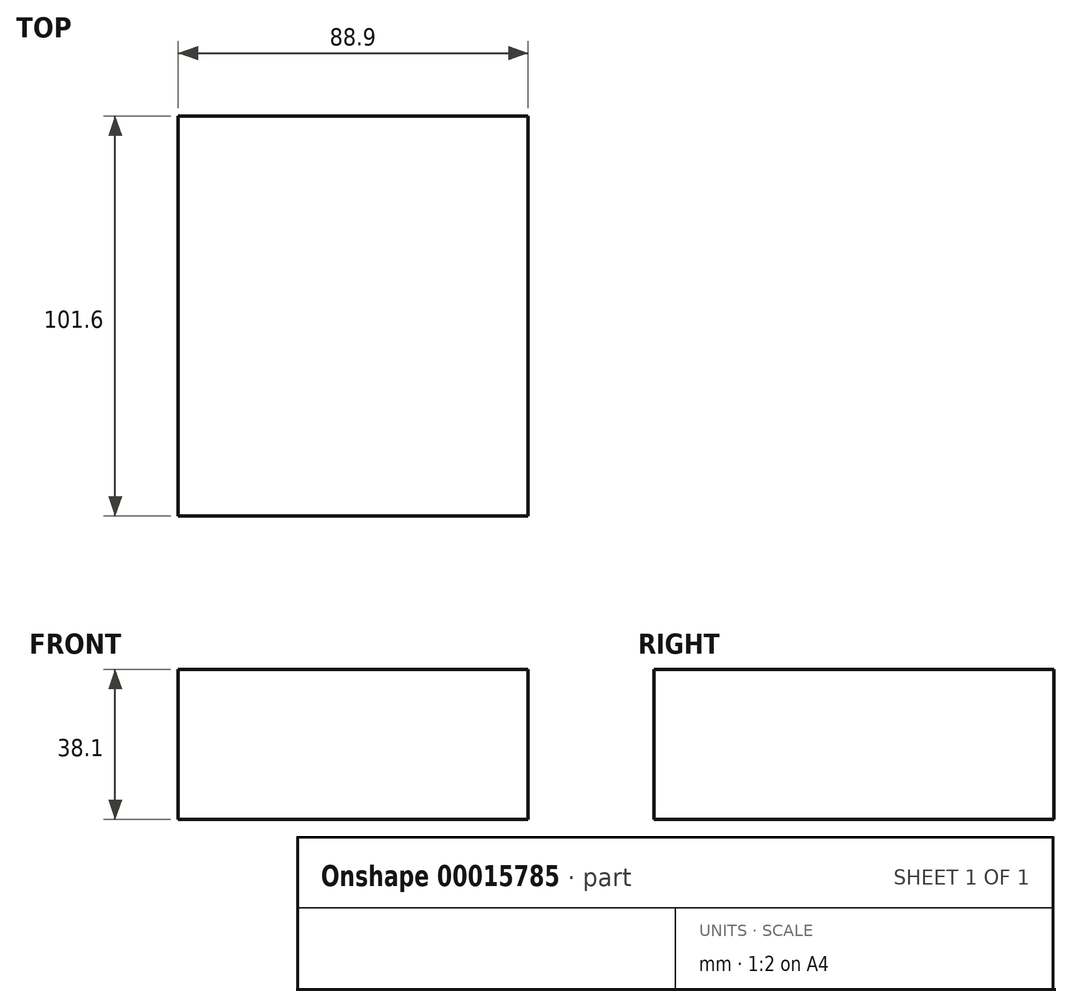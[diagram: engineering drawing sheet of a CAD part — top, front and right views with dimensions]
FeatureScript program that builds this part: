
annotation { "Feature Type Name" : "Feature", "Feature Type Description" : "" }
export const myFeature = defineFeature(function(context is Context, id is Id, definition is map)
    precondition{}
    {
        {
            var Q0;
            Q0=qCreatedBy(makeId("Top.planeOp"),FACE);
            var sketch = newSketch(context, id + "F0", { "sketchPlane" : qUnion([Q0])});
            skLineSegment(sketch, "E0.bottom", {"start": v(0, 0) * mm, "end": v(88.9, 0) * mm});
            skLineSegment(sketch, "E0.top", {"start": v(0, -101.6) * mm, "end": v(88.9, -101.6) * mm});
            skLineSegment(sketch, "E0.left", {"start": v(0, 0) * mm, "end": v(0, -101.6) * mm});
            skLineSegment(sketch, "E0.right", {"start": v(88.9, 0) * mm, "end": v(88.9, -101.6) * mm});
            skSolve(sketch);
        }
        {
            var Q0;
            Q0=qSketchRegion(id+"F0",true);
            extrude(context, id + "F1", {"entities" : qUnion([Q0]), "depth" : 38.1 * mm});
        }
    });
